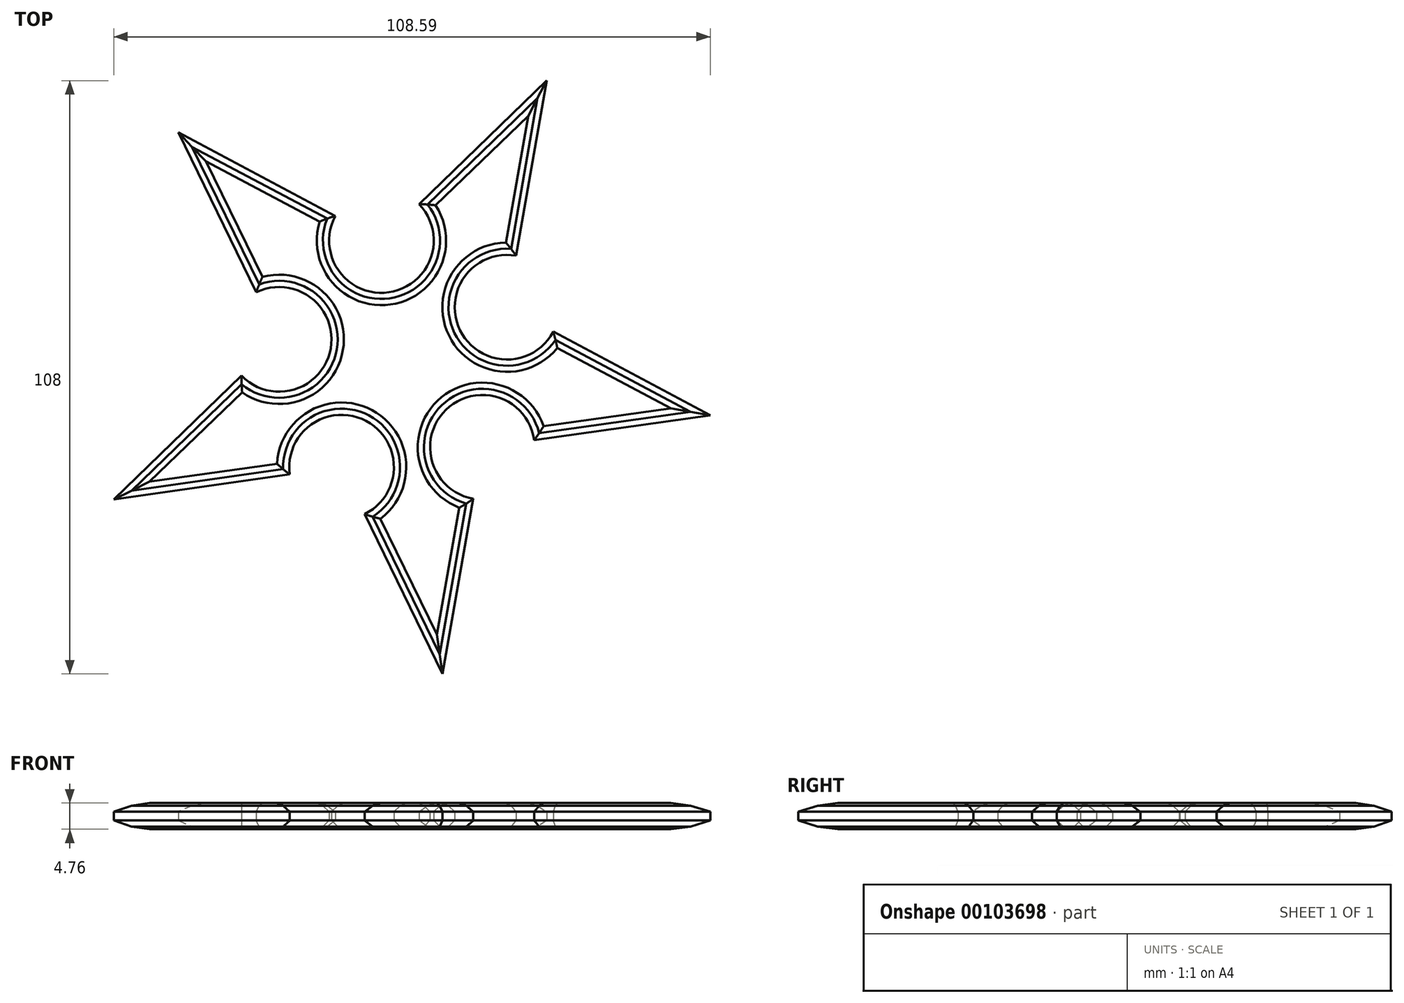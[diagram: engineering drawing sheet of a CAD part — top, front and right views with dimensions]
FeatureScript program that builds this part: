
annotation { "Feature Type Name" : "Feature", "Feature Type Description" : "" }
export const myFeature = defineFeature(function(context is Context, id is Id, definition is map)
    precondition{}
    {
        {
            var Q0;
            Q0=qCreatedBy(makeId("Top.planeOp"),FACE);
            var sketch = newSketch(context, id + "F0", { "sketchPlane" : qUnion([Q0])});
            skCircle(sketch, "E0.cCircle", {"center": v(0, 0) * mm, "radius": 46.64 * mm, "construction": true});
            skLineSegment(sketch, "E0.0", {"start": v(27.04, 50.91) * mm, "end": v(56.78, -9.99) * mm, "construction": true});
            skLineSegment(sketch, "E0.1", {"start": v(56.78, -9.99) * mm, "end": v(8.05, -57.09) * mm, "construction": true});
            skLineSegment(sketch, "E0.2", {"start": v(8.05, -57.09) * mm, "end": v(-51.8, -25.3) * mm, "construction": true});
            skLineSegment(sketch, "E0.3", {"start": v(-51.8, -25.3) * mm, "end": v(-40.07, 41.45) * mm, "construction": true});
            skLineSegment(sketch, "E0.4", {"start": v(-40.07, 41.45) * mm, "end": v(27.04, 50.91) * mm, "construction": true});
            skPoint(sketch, "E0.0.midPoint", {"position": v(41.91, 20.46) * mm});
            skLineSegment(sketch, "E1", {"start": v(-40.07, 41.45) * mm, "end": v(-21.69, 3.81) * mm});
            skLineSegment(sketch, "E2", {"start": v(27.04, 50.91) * mm, "end": v(19.79, 9.66) * mm});
            skLineSegment(sketch, "E3", {"start": v(-51.8, -25.3) * mm, "end": v(-10.33, -19.45) * mm});
            skLineSegment(sketch, "E4", {"start": v(-40.07, 41.45) * mm, "end": v(-3.07, 21.8) * mm});
            skLineSegment(sketch, "E5", {"start": v(-51.8, -25.3) * mm, "end": v(-21.69, 3.81) * mm});
            skLineSegment(sketch, "E6.trimOffspring", {"start": v(-3.07, 21.8) * mm, "end": v(27.04, 50.91) * mm});
            skLineSegment(sketch, "E7.trimOffspring", {"start": v(-10.33, -19.45) * mm, "end": v(8.05, -57.09) * mm});
            skLineSegment(sketch, "E8.trimOffspring", {"start": v(19.79, 9.66) * mm, "end": v(56.78, -9.99) * mm});
            skLineSegment(sketch, "E9.trimOffspring", {"start": v(15.3, -15.83) * mm, "end": v(8.05, -57.09) * mm});
            skLineSegment(sketch, "E10.trimOffspring", {"start": v(15.3, -15.83) * mm, "end": v(56.78, -9.99) * mm});
            skSolve(sketch);
        }
        {
            var Q0;
            Q0 = qSketchRegion(id + "F0", true);
            extrude(context, id + "F1", {"entities" : qUnion([Q0]), "depth" : 4.76 * mm});
        }
        {
            var Q0;
            Q0=qCreatedBy(makeId("Top.planeOp"),FACE);
            var sketch = newSketch(context, id + "F2", { "sketchPlane" : qUnion([Q0])});
            skCircle(sketch, "E11", {"center": v(15.3, -15.83) * mm, "radius": 9.53 * mm});
            skCircle(sketch, "E12", {"center": v(-10.33, -19.45) * mm, "radius": 9.53 * mm});
            skCircle(sketch, "E13", {"center": v(-21.69, 3.81) * mm, "radius": 9.53 * mm});
            skCircle(sketch, "E14", {"center": v(-3.07, 21.8) * mm, "radius": 9.53 * mm});
            skCircle(sketch, "E15", {"center": v(19.79, 9.66) * mm, "radius": 9.53 * mm});
            skSolve(sketch);
        }
        {
            var Q0;
            Q0 = qSketchRegion(id + "F2", true);
            extrude(context, id + "F3", {"entities" : qUnion([Q0]), "operationType" : NewBodyOperationType.REMOVE, "endBound" : BoundingType.THROUGH_ALL, "depth" : 25.4 * mm});
        }
        {
            var Q0;
            Q0=makeQuery(id+"F1.opExtrude","CAP_FACE",FACE,{"disambiguationData":[OSD([sQuery(id+"F0.wireOp",EDGE,"E1"),sQuery(id+"F0.wireOp",EDGE,"E2"),sQuery(id+"F0.wireOp",EDGE,"E3"),sQuery(id+"F0.wireOp",EDGE,"E4"),sQuery(id+"F0.wireOp",EDGE,"E5"),sQuery(id+"F0.wireOp",EDGE,"E6.trimOffspring"),sQuery(id+"F0.wireOp",EDGE,"E7.trimOffspring"),sQuery(id+"F0.wireOp",EDGE,"E8.trimOffspring"),sQuery(id+"F0.wireOp",EDGE,"E9.trimOffspring"),sQuery(id+"F0.wireOp",EDGE,"E10.trimOffspring")])],"isStart":false});
            var Q1;
            Q1=makeQuery(id+"F1.opExtrude","CAP_FACE",FACE,{"disambiguationData":[OSD([sQuery(id+"F0.wireOp",EDGE,"E1"),sQuery(id+"F0.wireOp",EDGE,"E2"),sQuery(id+"F0.wireOp",EDGE,"E3"),sQuery(id+"F0.wireOp",EDGE,"E4"),sQuery(id+"F0.wireOp",EDGE,"E5"),sQuery(id+"F0.wireOp",EDGE,"E6.trimOffspring"),sQuery(id+"F0.wireOp",EDGE,"E7.trimOffspring"),sQuery(id+"F0.wireOp",EDGE,"E8.trimOffspring"),sQuery(id+"F0.wireOp",EDGE,"E9.trimOffspring"),sQuery(id+"F0.wireOp",EDGE,"E10.trimOffspring")])],"isStart":true});
            chamfer(context, id + "F4", {"entities" : qUnion([Q0, Q1]), "width" : 1.59 * mm, "tangentPropagation" : true});
        }
        {
            var Q0;
            Q0=makeQuery(id+"F1.opExtrude","CAP_FACE",FACE,{"disambiguationData":[OSD([sQuery(id+"F0.wireOp",EDGE,"E1"),sQuery(id+"F0.wireOp",EDGE,"E2"),sQuery(id+"F0.wireOp",EDGE,"E3"),sQuery(id+"F0.wireOp",EDGE,"E4"),sQuery(id+"F0.wireOp",EDGE,"E5"),sQuery(id+"F0.wireOp",EDGE,"E6.trimOffspring"),sQuery(id+"F0.wireOp",EDGE,"E7.trimOffspring"),sQuery(id+"F0.wireOp",EDGE,"E8.trimOffspring"),sQuery(id+"F0.wireOp",EDGE,"E9.trimOffspring"),sQuery(id+"F0.wireOp",EDGE,"E10.trimOffspring")])],"isStart":false});
            var Q1;
            Q1=makeQuery(id+"F1.opExtrude","CAP_FACE",FACE,{"disambiguationData":[OSD([sQuery(id+"F0.wireOp",EDGE,"E1"),sQuery(id+"F0.wireOp",EDGE,"E2"),sQuery(id+"F0.wireOp",EDGE,"E3"),sQuery(id+"F0.wireOp",EDGE,"E4"),sQuery(id+"F0.wireOp",EDGE,"E5"),sQuery(id+"F0.wireOp",EDGE,"E6.trimOffspring"),sQuery(id+"F0.wireOp",EDGE,"E7.trimOffspring"),sQuery(id+"F0.wireOp",EDGE,"E8.trimOffspring"),sQuery(id+"F0.wireOp",EDGE,"E9.trimOffspring"),sQuery(id+"F0.wireOp",EDGE,"E10.trimOffspring")])],"isStart":true});
            chamfer(context, id + "F5", {"entities" : qUnion([Q0, Q1]), "width" : 1.59 * mm, "tangentPropagation" : true});
        }
    });
